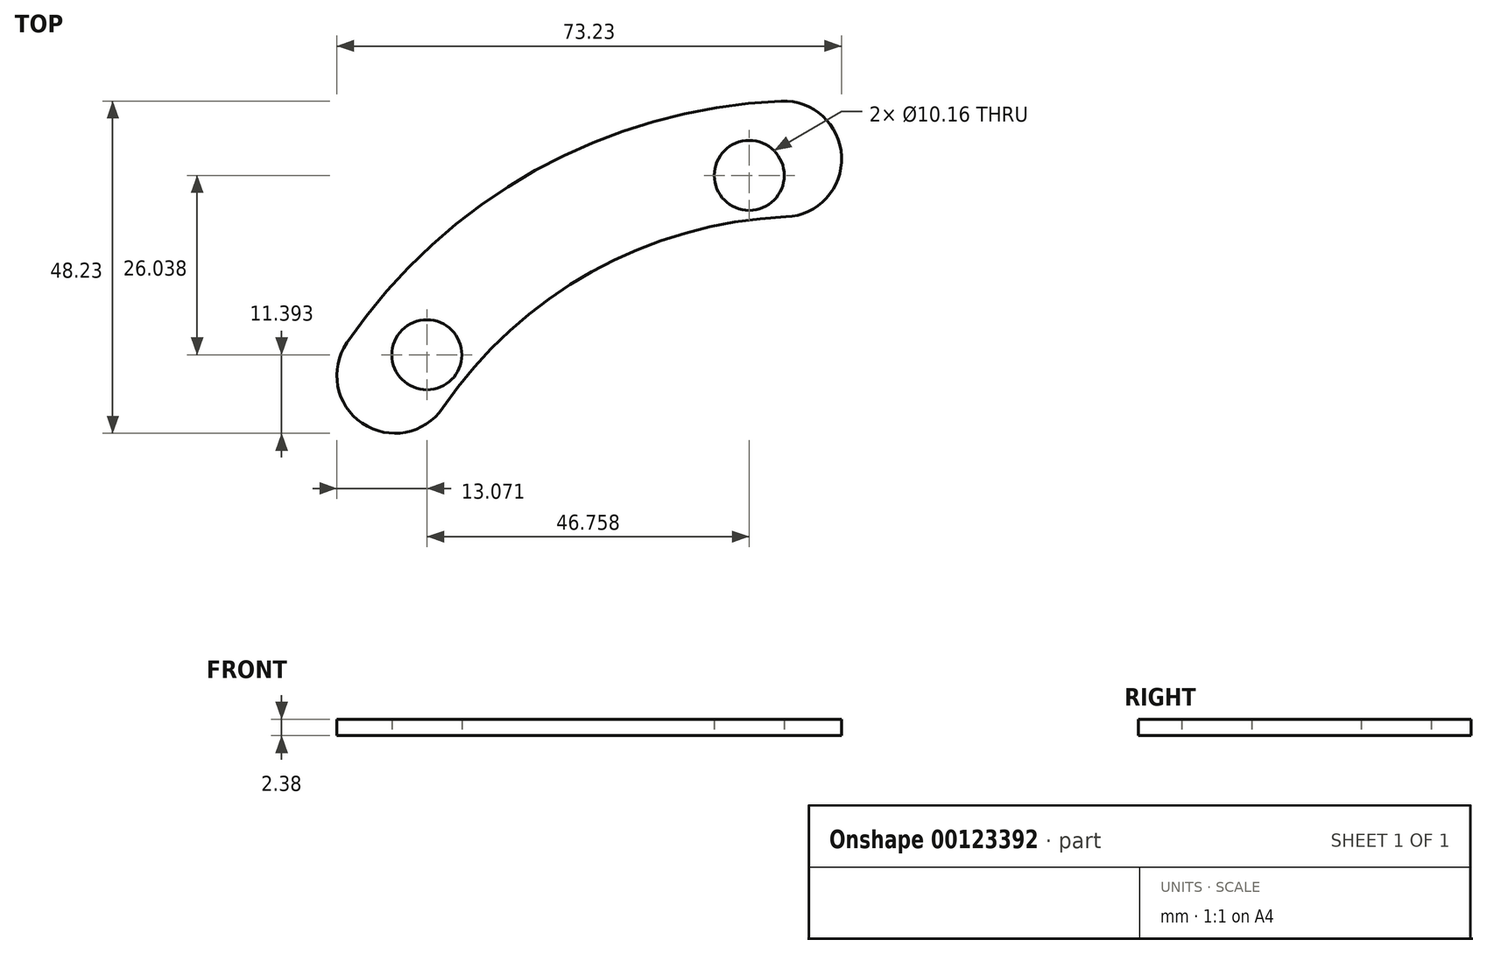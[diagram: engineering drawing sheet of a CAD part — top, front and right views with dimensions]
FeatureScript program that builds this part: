
annotation { "Feature Type Name" : "Feature", "Feature Type Description" : "" }
export const myFeature = defineFeature(function(context is Context, id is Id, definition is map)
    precondition{}
    {
        {
            var Q0;
            Q0=qCreatedBy(makeId("Top.planeOp"),FACE);
            var sketch = newSketch(context, id + "F0", { "sketchPlane" : qUnion([Q0])});
            skArc(sketch, "E0", {"start": v(-2.7, 63.44) * mm, "mid": v(-30.9, 55.48) * mm, "end": v(-52.5, 35.71) * mm});
            skArc(sketch, "E1", {"start": v(-3.43, 80.25) * mm, "mid": v(-39.08, 70.18) * mm, "end": v(-66.42, 45.17) * mm});
            skCircle(sketch, "E2", {"center": v(0, 0) * mm, "radius": 69.93 * mm, "construction": true});
            skCircle(sketch, "E3", {"center": v(0, 0) * mm, "radius": 62.55 * mm, "construction": true});
            skCircle(sketch, "E4", {"center": v(-54.8, 43.42) * mm, "radius": 5.08 * mm});
            skCircle(sketch, "E5", {"center": v(-8.05, 69.46) * mm, "radius": 5.08 * mm});
            skLineSegment(sketch, "E6", {"start": v(-8.05, 69.46) * mm, "end": v(0, 0) * mm, "construction": true});
            skLineSegment(sketch, "E7", {"start": v(0, 0) * mm, "end": v(-54.8, 43.42) * mm, "construction": true});
            skLineSegment(sketch, "E8", {"start": v(-52.5, 35.71) * mm, "end": v(-66.42, 45.17) * mm, "construction": true});
            skPoint(sketch, "E9", {"position": v(-59.46, 40.44) * mm});
            skArc(sketch, "E10", {"start": v(-66.42, 45.17) * mm, "mid": v(-64.2, 33.49) * mm, "end": v(-52.5, 35.71) * mm});
            skLineSegment(sketch, "E11", {"start": v(-3.43, 80.25) * mm, "end": v(-2.7, 63.44) * mm, "construction": true});
            skPoint(sketch, "E12.orphan", {"position": v(-2.67, 62.5) * mm});
            skPoint(sketch, "E13", {"position": v(-3.07, 71.85) * mm});
            skArc(sketch, "E14.trimOffspring", {"start": v(-2.7, 63.44) * mm, "mid": v(5.34, 72.2) * mm, "end": v(-3.43, 80.25) * mm});
            skPoint(sketch, "E15.orphan", {"position": v(0, 63.5) * mm});
            skSolve(sketch);
        }
        {
            var Q0;
            Q0 = qSketchRegion(id + "F0", true);
            extrude(context, id + "F1", {"entities" : qUnion([Q0]), "depth" : 2.38 * mm});
        }
    });
